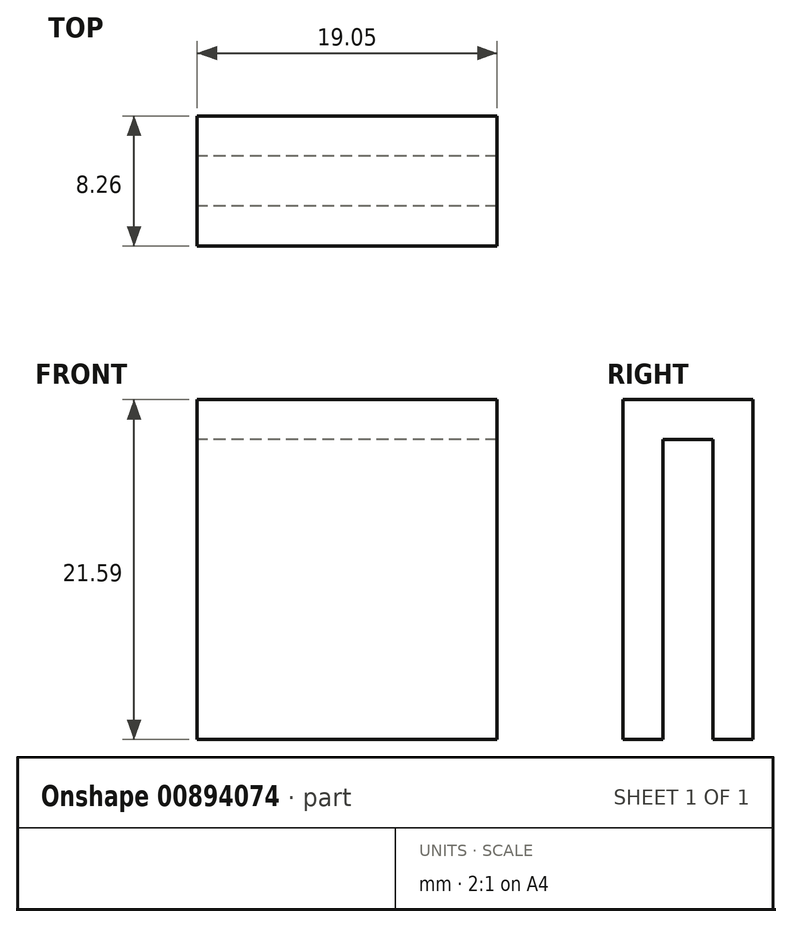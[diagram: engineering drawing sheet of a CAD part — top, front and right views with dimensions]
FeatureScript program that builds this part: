
annotation { "Feature Type Name" : "Feature", "Feature Type Description" : "" }
export const myFeature = defineFeature(function(context is Context, id is Id, definition is map)
    precondition{}
    {
        {
            var Q0;
            Q0=qCreatedBy(makeId("Right.planeOp"),FACE);
            var sketch = newSketch(context, id + "F0", { "sketchPlane" : qUnion([Q0])});
            skLineSegment(sketch, "E0.bottom", {"start": v(-7.26, 21.59) * mm, "end": v(1, 21.59) * mm});
            skLineSegment(sketch, "E0.top", {"start": v(-7.26, 0) * mm, "end": v(-4.72, 0) * mm});
            skLineSegment(sketch, "E0.left", {"start": v(-7.26, 21.6) * mm, "end": v(-7.26, 0) * mm});
            skLineSegment(sketch, "E0.right", {"start": v(1, 21.6) * mm, "end": v(1, 0) * mm});
            skLineSegment(sketch, "E1.top", {"start": v(-4.72, 19.05) * mm, "end": v(-1.54, 19.05) * mm});
            skLineSegment(sketch, "E1.left", {"start": v(-4.72, 0) * mm, "end": v(-4.72, 19.05) * mm});
            skLineSegment(sketch, "E1.right", {"start": v(-1.54, 0) * mm, "end": v(-1.54, 19.05) * mm});
            skPoint(sketch, "E2", {"position": v(-3.13, 19.05) * mm});
            skPoint(sketch, "E3", {"position": v(-3.13, 21.59) * mm});
            skLineSegment(sketch, "E4.trimOffspring", {"start": v(-1.54, 0) * mm, "end": v(1, 0) * mm});
            skSolve(sketch);
        }
        {
            var Q0;
            Q0 = qSketchRegion(id + "F0", true);
            extrude(context, id + "F1", {"entities" : qUnion([Q0]), "depth" : 19.05 * mm, "offsetDistance" : 25.4 * mm});
        }
    });
